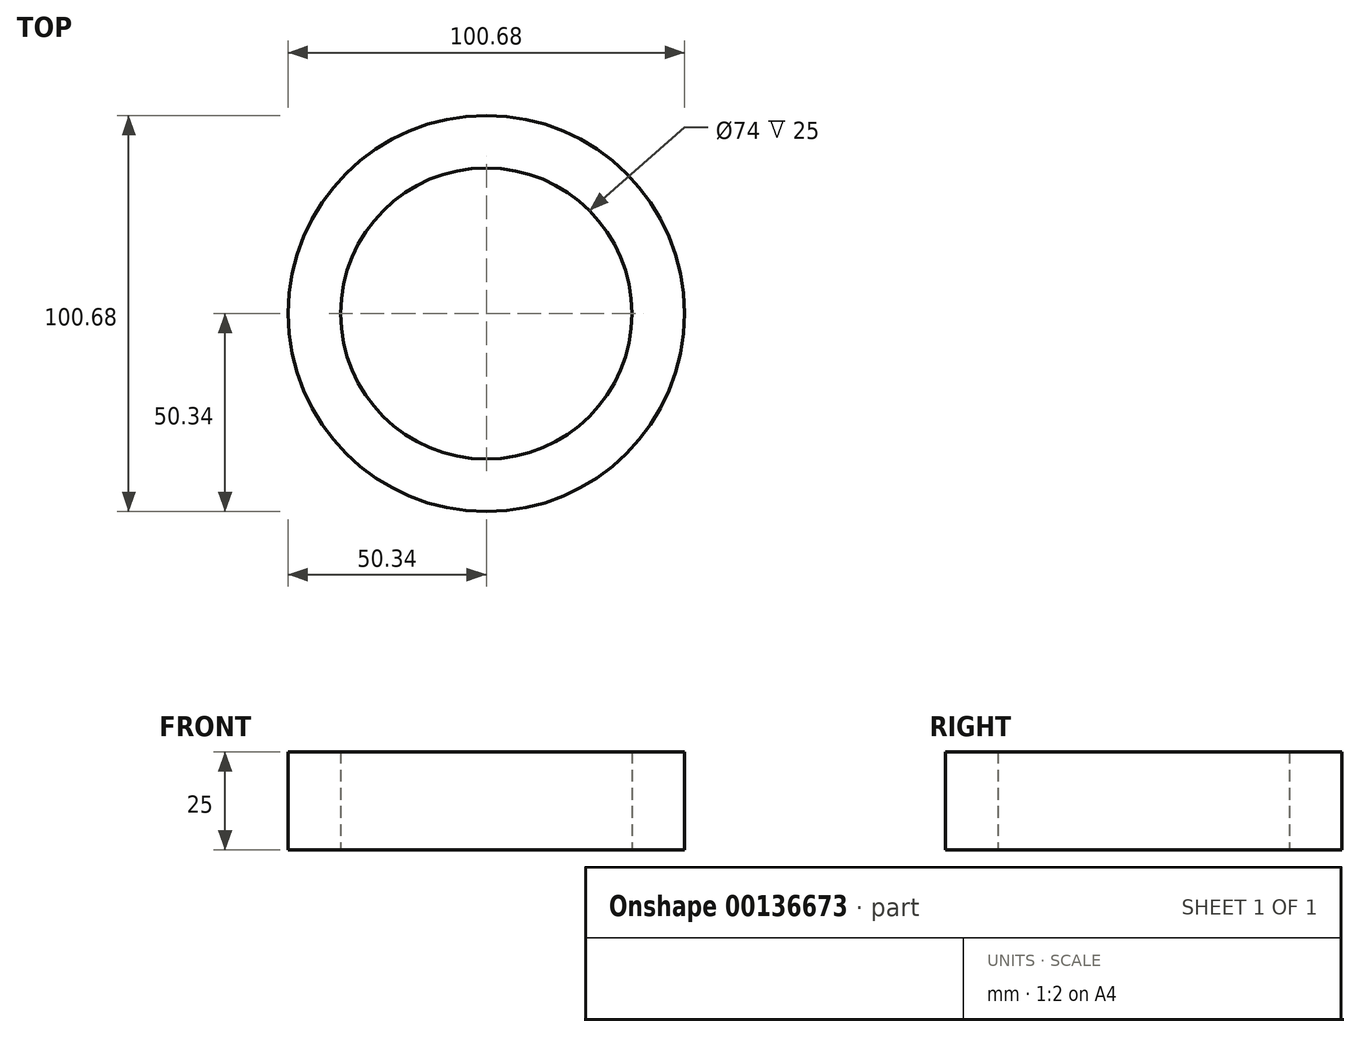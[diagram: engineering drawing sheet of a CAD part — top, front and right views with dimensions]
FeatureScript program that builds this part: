
annotation { "Feature Type Name" : "Feature", "Feature Type Description" : "" }
export const myFeature = defineFeature(function(context is Context, id is Id, definition is map)
    precondition{}
    {
        {
            var Q0;
            Q0=qCreatedBy(makeId("Top.planeOp"),FACE);
            var sketch = newSketch(context, id + "F0", { "sketchPlane" : qUnion([Q0])});
            skCircle(sketch, "E0", {"center": v(0, 0) * mm, "radius": 37 * mm});
            skCircle(sketch, "E1", {"center": v(0, 0) * mm, "radius": 50.34 * mm});
            skSolve(sketch);
        }
        {
            var Q0;
            Q0=makeQuery(id+"F0.imprint","IMPRINT",FACE,{"disambiguationData":[TD([[makeQuery(id+"F0.imprint","IMPRINT",EDGE,{"derivedFrom":sQuery(id+"F0.wireOp",EDGE,"E0")}),-1.0]])]});
            extrude(context, id + "F1", {"entities" : qUnion([Q0]), "depth" : 25 * mm});
        }
    });
